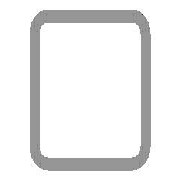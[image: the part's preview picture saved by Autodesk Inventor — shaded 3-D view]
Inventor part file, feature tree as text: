
AUTODESK INVENTOR PART (.ipt)
format: ipt  version: 2025 (Build 290162010, 162A)  size: 133,632 bytes
history: native  units: mm (DEFAULTED — no unit token found)
features: other x4, sketch x1, plane x1
ambient origin geometry x8: Origin, YZ Plane, XZ Plane, XY Plane, X Axis, Y Axis, Z Axis, Center Point
bodies: Solid1 (feature_tree), Body (feature_tree)
feature tree (6):
  parser-record x1  (decoder bookkeeping rows leaked as tree rows — omitted from the tree; the rows remain in map.json)
  other  "Driven Length"
  other  "Start Plane"
  other  "End Plane"
  sketch  "Sketch3"  dims[d3=3290.0mm d4=0.0mm d7=6.0mm d9=80.0mm d11=80.0mm d12=3.0mm d13=-0.0mm d14=3290.0mm d15=40.0mm d16=40.0mm d17=90.0deg d18=3290.0mm]
  plane  "Work Plane3"
